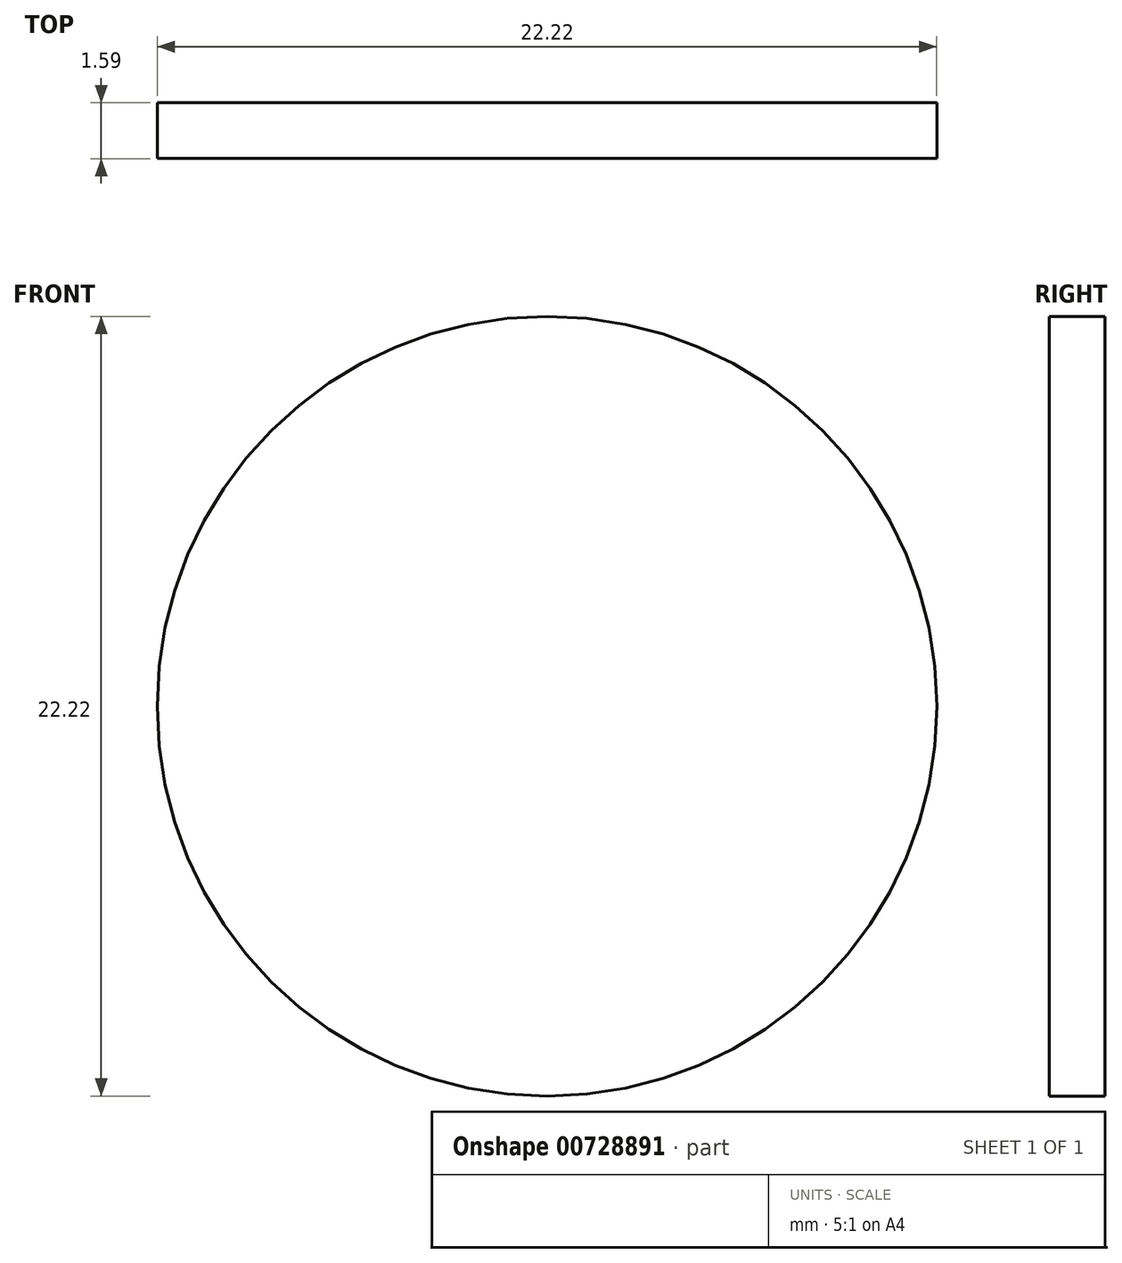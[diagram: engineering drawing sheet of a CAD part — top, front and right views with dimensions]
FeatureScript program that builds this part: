
annotation { "Feature Type Name" : "Feature", "Feature Type Description" : "" }
export const myFeature = defineFeature(function(context is Context, id is Id, definition is map)
    precondition{}
    {
        {
            var Q0;
            Q0=qCreatedBy(makeId("Front.planeOp"),FACE);
            var sketch = newSketch(context, id + "F0", { "sketchPlane" : qUnion([Q0])});
            skCircle(sketch, "E0", {"center": v(0, 0) * mm, "radius": 11.11 * mm});
            skSolve(sketch);
        }
        {
            var Q0;
            Q0 = qSketchRegion(id + "F0", true);
            extrude(context, id + "F1", {"entities" : qUnion([Q0]), "depth" : 1.59 * mm, "offsetDistance" : 25.4 * mm});
        }
    });
